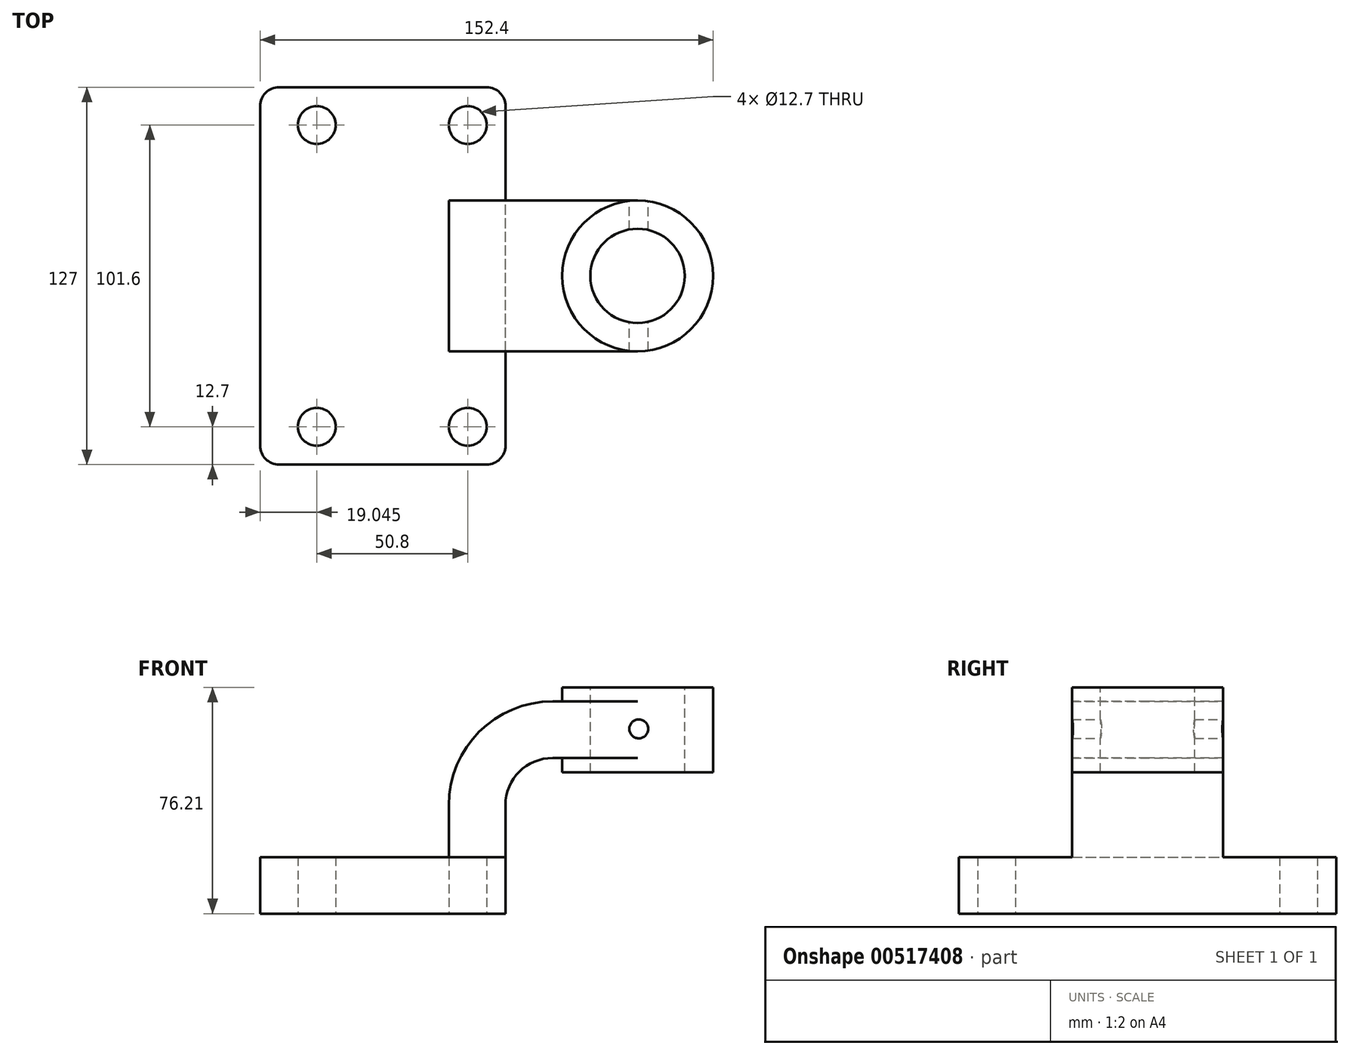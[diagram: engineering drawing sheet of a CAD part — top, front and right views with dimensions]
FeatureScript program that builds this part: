
annotation { "Feature Type Name" : "Feature", "Feature Type Description" : "" }
export const myFeature = defineFeature(function(context is Context, id is Id, definition is map)
    precondition{}
    {
        {
            var Q0;
            Q0=qCreatedBy(makeId("Front.planeOp"),FACE);
            var sketch = newSketch(context, id + "F0", { "sketchPlane" : qUnion([Q0])});
            skLineSegment(sketch, "E0.bottom", {"start": v(-41.28, -9.53) * mm, "end": v(41.28, -9.53) * mm});
            skLineSegment(sketch, "E0.top", {"start": v(-41.28, 9.53) * mm, "end": v(41.28, 9.53) * mm});
            skLineSegment(sketch, "E0.left", {"start": v(-41.28, -9.53) * mm, "end": v(-41.28, 9.53) * mm});
            skLineSegment(sketch, "E0.right", {"start": v(41.28, -9.53) * mm, "end": v(41.28, 9.53) * mm});
            skPoint(sketch, "E0.middle", {"position": v(0, 0) * mm});
            skLineSegment(sketch, "E1.bottom", {"start": v(60.32, 38.1) * mm, "end": v(111.12, 38.1) * mm});
            skLineSegment(sketch, "E1.top", {"start": v(60.32, 66.67) * mm, "end": v(111.12, 66.67) * mm});
            skLineSegment(sketch, "E1.left", {"start": v(60.32, 38.1) * mm, "end": v(60.32, 66.67) * mm});
            skLineSegment(sketch, "E1.right", {"start": v(111.12, 38.1) * mm, "end": v(111.12, 66.67) * mm});
            skPoint(sketch, "E1.middle", {"position": v(85.72, 52.39) * mm});
            skLineSegment(sketch, "E2", {"start": v(41.28, 9.53) * mm, "end": v(41.28, 27) * mm});
            skArc(sketch, "E3", {"start": v(41.27, 27) * mm, "mid": v(45.92, 38.23) * mm, "end": v(57.15, 42.88) * mm});
            skLineSegment(sketch, "E4", {"start": v(57.15, 42.88) * mm, "end": v(85.72, 42.88) * mm});
            skPoint(sketch, "E4.endSnap0", {"position": v(85.72, 38.1) * mm});
            skLineSegment(sketch, "E5.0", {"start": v(57.15, 61.93) * mm, "end": v(85.72, 61.93) * mm});
            skArc(sketch, "E5.1", {"start": v(22.22, 27) * mm, "mid": v(32.45, 51.7) * mm, "end": v(57.15, 61.93) * mm});
            skLineSegment(sketch, "E5.2", {"start": v(22.22, 9.53) * mm, "end": v(22.22, 27) * mm});
            skLineSegment(sketch, "E6", {"start": v(85.72, 38.1) * mm, "end": v(85.72, 66.67) * mm});
            skFitSpline(sketch, "E7", {"points": [v(-41.28, 9.53) * mm, v(57.15, 61.93) * mm], "startDerivative": vector(65.85, 76.84) * mm, "endDerivative": vector(106.92, -17.93) * mm});
            skSolve(sketch);
        }
        {
            var Q0;
            Q0=makeQuery(id+"F0.imprint","IMPRINT",FACE,{"disambiguationData":[TD([[makeQuery(id+"F0.imprint","IMPRINT",EDGE,{"derivedFrom":sQuery(id+"F0.wireOp",EDGE,"E0.bottom")}),1.0]])]});
            extrude(context, id + "F1", {"entities" : qUnion([Q0]), "endBound" : BoundingType.SYMMETRIC, "depth" : 127 * mm});
        }
        {
            var Q0;
            {var subQ1=sQuery(id+"F0.wireOp",EDGE,"E2");Q0=makeQuery(id+"F0.imprint","IMPRINT",FACE,{"disambiguationData":[TD([[makeQuery(id+"F0.imprint","IMPRINT",EDGE,{"derivedFrom":subQ1}),1.0]])]});}
            var Q1;
            {var subQ0=sQuery(id+"F0.wireOp",EDGE,"E4");var subQ1=sQuery(id+"F0.wireOp",EDGE,"E1.left");var subQ2=makeQuery(id+"F0.imprint","INTERSECT",VERTEX,{"derivedFrom":[subQ1,subQ0]});Q1=makeQuery(id+"F0.imprint","IMPRINT",FACE,{"disambiguationData":[TD([[makeQuery(id+"F0.imprint","IMPRINT",EDGE,{"disambiguationData":[TD([[subQ2,-1.0]])],"derivedFrom":subQ1}),-1.0]])]});}
            extrude(context, id + "F2", {"entities" : qUnion([Q0, Q1]), "operationType" : NewBodyOperationType.ADD, "endBound" : BoundingType.SYMMETRIC, "depth" : 50.8 * mm});
        }
        {
            var Q0;
            Q0=makeQuery(id+"F0.imprint","IMPRINT",FACE,{"disambiguationData":[TD([[makeQuery(id+"F0.imprint","IMPRINT",EDGE,{"derivedFrom":sQuery(id+"F0.wireOp",EDGE,"E5.1")}),1.0]])]});
            extrude(context, id + "F3", {"entities" : qUnion([Q0]), "operationType" : NewBodyOperationType.ADD, "endBound" : BoundingType.SYMMETRIC, "depth" : 15.88 * mm});
        }
        {
            var Q0;
            {var subQ0=sQuery(id+"F0.wireOp",EDGE,"E1.right");Q0=makeQuery(id+"F0.imprint","IMPRINT",FACE,{"disambiguationData":[TD([[makeQuery(id+"F0.imprint","IMPRINT",EDGE,{"derivedFrom":subQ0}),1.0]])]});}
            var Q1;
            Q1=sQuery(id+"F0.wireOp",EDGE,"E6");
            revolve(context, id + "F4", {"operationType" : NewBodyOperationType.ADD, "entities" : qUnion([Q0]), "axis" : qUnion([Q1]), "revolveType" : RevolveType.FULL});
        }
        {
            var Q0;
            Q0=makeQuery(id+"F1.opExtrude","CAP_EDGE",EDGE,{"disambiguationData":[OSD([sQuery(id+"F0.wireOp",EDGE,"E0.left")])],"isStart":false});
            var Q1;
            Q1=makeQuery(id+"F1.opExtrude","CAP_EDGE",EDGE,{"disambiguationData":[OSD([sQuery(id+"F0.wireOp",EDGE,"E0.right")])],"isStart":false});
            var Q2;
            Q2=makeQuery(id+"F1.opExtrude","CAP_EDGE",EDGE,{"disambiguationData":[OSD([sQuery(id+"F0.wireOp",EDGE,"E0.right")])],"isStart":true});
            var Q3;
            Q3=makeQuery(id+"F1.opExtrude","CAP_EDGE",EDGE,{"disambiguationData":[OSD([sQuery(id+"F0.wireOp",EDGE,"E0.left")])],"isStart":true});
            fillet(context, id + "F5", {"entities" : qUnion([Q0, Q1, Q2, Q3]), "radius" : 6.35 * mm, "tangentPropagation" : true, "allowEdgeOverflow" : false});
        }
        {
            var Q0;
            Q0=makeQuery(id+"F4.opRevolve","SWEPT_FACE",FACE,{"disambiguationData":[OSD([sQuery(id+"F0.wireOp",EDGE,"E1.top")])]});
            var sketch = newSketch(context, id + "F6", { "sketchPlane" : qUnion([Q0])});
            skCircle(sketch, "E8", {"center": v(85.72, 0) * mm, "radius": 15.88 * mm});
            skSolve(sketch);
        }
        {
            var Q0;
            Q0 = qSketchRegion(id + "F6", true);
            extrude(context, id + "F7", {"entities" : qUnion([Q0]), "operationType" : NewBodyOperationType.REMOVE, "endBound" : BoundingType.THROUGH_ALL, "oppositeDirection" : true, "depth" : 25.4 * mm});
        }
        {
            var Q0;
            Q0=makeQuery(id+"F1.opExtrude","SWEPT_FACE",FACE,{"disambiguationData":[OSD([sQuery(id+"F0.wireOp",EDGE,"E0.bottom")])]});
            var sketch = newSketch(context, id + "F8", { "sketchPlane" : qUnion([Q0])});
            skCircle(sketch, "E9", {"center": v(28.58, 50.8) * mm, "radius": 6.35 * mm});
            skCircle(sketch, "E10", {"center": v(-22.23, 50.8) * mm, "radius": 6.35 * mm});
            skCircle(sketch, "E11", {"center": v(-22.22, -50.8) * mm, "radius": 6.35 * mm});
            skCircle(sketch, "E12", {"center": v(28.58, -50.8) * mm, "radius": 6.35 * mm});
            skSolve(sketch);
        }
        {
            var Q0;
            Q0 = qSketchRegion(id + "F8", true);
            extrude(context, id + "F9", {"entities" : qUnion([Q0]), "operationType" : NewBodyOperationType.REMOVE, "endBound" : BoundingType.THROUGH_ALL, "oppositeDirection" : true, "depth" : 25.4 * mm});
        }
        {
            var Q0;
            {var subQ0=sQuery(id+"F0.wireOp",EDGE,"E1.left");var subQ1=sQuery(id+"F0.wireOp",EDGE,"E1.top");var subQ2=makeQuery(id+"F0.imprint","INTERSECT",VERTEX,{"derivedFrom":[subQ1,subQ0]});Q0=makeQuery(id+"F0.imprint","IMPRINT",FACE,{"disambiguationData":[TD([[makeQuery(id+"F0.imprint","IMPRINT",EDGE,{"disambiguationData":[TD([[subQ2,-1.0]])],"derivedFrom":subQ1}),-1.0]])]});}
            var sketch = newSketch(context, id + "F10", { "sketchPlane" : qUnion([Q0])});
            skCircle(sketch, "E13", {"center": v(86.13, 52.66) * mm, "radius": 3.18 * mm});
            skSolve(sketch);
        }
        {
            var Q0;
            Q0 = qSketchRegion(id + "F10", true);
            extrude(context, id + "F11", {"entities" : qUnion([Q0]), "operationType" : NewBodyOperationType.REMOVE, "endBound" : BoundingType.SYMMETRIC, "depth" : 63.5 * mm});
        }
    });
